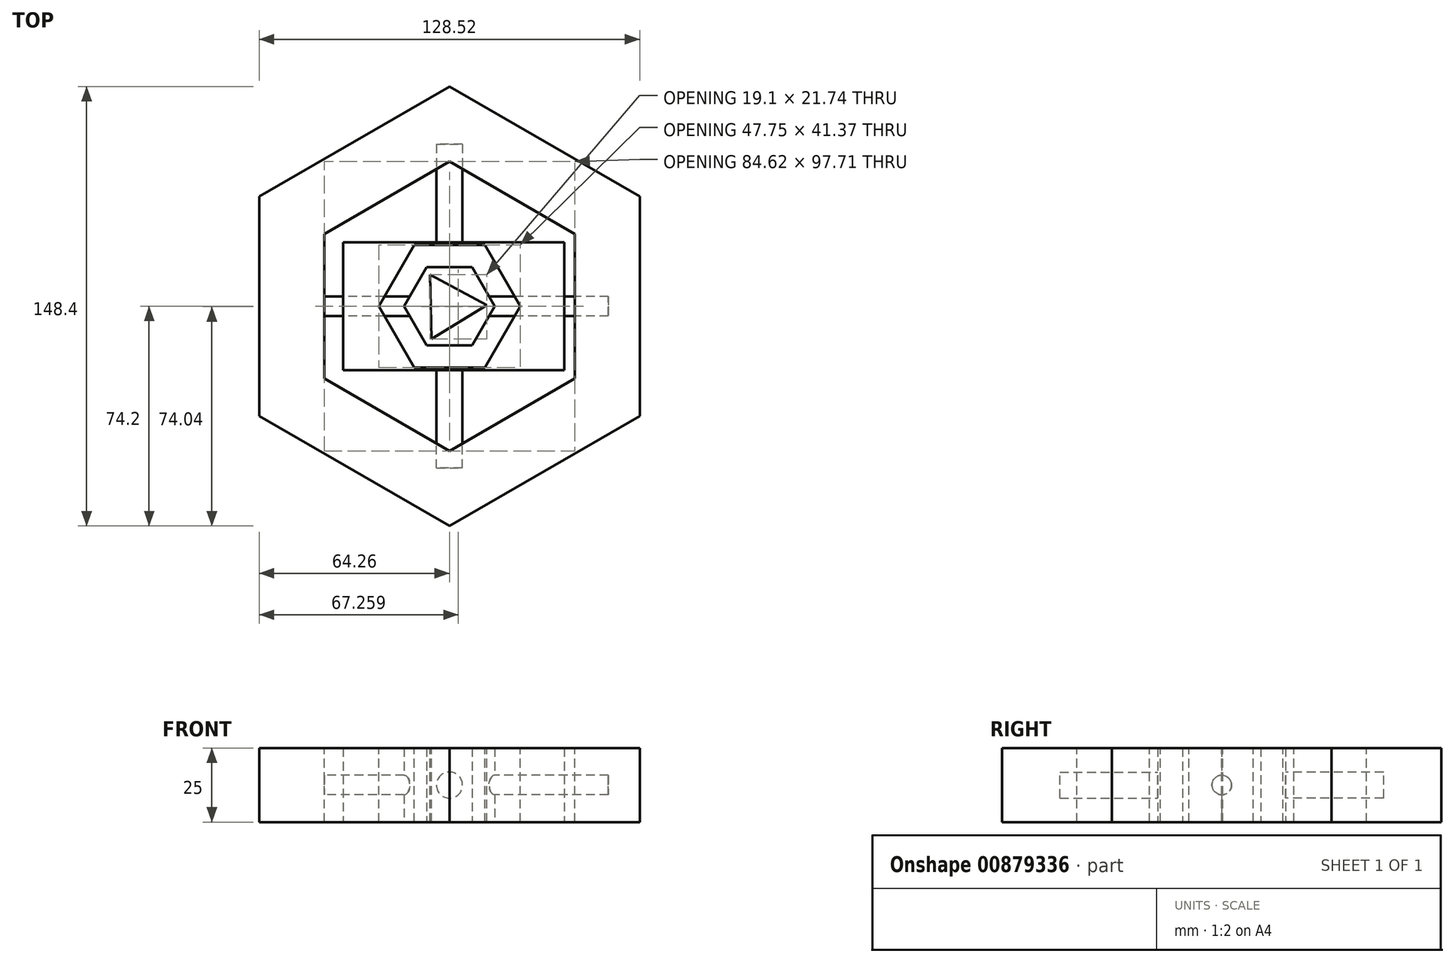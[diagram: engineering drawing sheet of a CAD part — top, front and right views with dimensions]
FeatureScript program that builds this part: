
annotation { "Feature Type Name" : "Feature", "Feature Type Description" : "" }
export const myFeature = defineFeature(function(context is Context, id is Id, definition is map)
    precondition{}
    {
        {
            var Q0;
            Q0=qCreatedBy(makeId("Top.planeOp"),FACE);
            var sketch = newSketch(context, id + "F0", { "sketchPlane" : qUnion([Q0])});
            skCircle(sketch, "E0.cCircle", {"center": v(0, 0) * mm, "radius": 74.2 * mm, "construction": true});
            skLineSegment(sketch, "E0.0", {"start": v(0, 74.2) * mm, "end": v(64.26, 37.1) * mm});
            skLineSegment(sketch, "E0.1", {"start": v(64.26, 37.1) * mm, "end": v(64.26, -37.1) * mm});
            skLineSegment(sketch, "E0.2", {"start": v(64.26, -37.1) * mm, "end": v(0, -74.2) * mm});
            skLineSegment(sketch, "E0.3", {"start": v(0, -74.2) * mm, "end": v(-64.26, -37.1) * mm});
            skLineSegment(sketch, "E0.4", {"start": v(-64.26, -37.1) * mm, "end": v(-64.26, 37.1) * mm});
            skLineSegment(sketch, "E0.5", {"start": v(-64.26, 37.1) * mm, "end": v(0, 74.2) * mm});
            skSolve(sketch);
        }
        {
            var Q0;
            Q0 = qSketchRegion(id + "F0", true);
            extrude(context, id + "F1", {"entities" : qUnion([Q0]), "depth" : 25 * mm, "offsetDistance" : 25 * mm});
        }
        {
            var Q0;
            Q0=makeQuery(id+"F1.opExtrude","CAP_FACE",FACE,{"disambiguationData":[OSD([sQuery(id+"F0.wireOp",EDGE,"E0.0"),sQuery(id+"F0.wireOp",EDGE,"E0.1"),sQuery(id+"F0.wireOp",EDGE,"E0.2"),sQuery(id+"F0.wireOp",EDGE,"E0.3"),sQuery(id+"F0.wireOp",EDGE,"E0.4"),sQuery(id+"F0.wireOp",EDGE,"E0.5")])],"isStart":false});
            var sketch = newSketch(context, id + "F2", { "sketchPlane" : qUnion([Q0])});
            skCircle(sketch, "E1.cCircle", {"center": v(0, 0) * mm, "radius": 48.86 * mm, "construction": true});
            skLineSegment(sketch, "E1.0", {"start": v(0, 48.86) * mm, "end": v(42.31, 24.43) * mm});
            skLineSegment(sketch, "E1.1", {"start": v(42.31, 24.43) * mm, "end": v(42.31, -24.43) * mm});
            skLineSegment(sketch, "E1.2", {"start": v(42.31, -24.43) * mm, "end": v(0, -48.86) * mm});
            skLineSegment(sketch, "E1.3", {"start": v(0, -48.86) * mm, "end": v(-42.31, -24.43) * mm});
            skLineSegment(sketch, "E1.4", {"start": v(-42.31, -24.43) * mm, "end": v(-42.31, 24.43) * mm});
            skLineSegment(sketch, "E1.5", {"start": v(-42.31, 24.43) * mm, "end": v(0, 48.86) * mm});
            skSolve(sketch);
        }
        {
            var Q0;
            Q0 = qSketchRegion(id + "F2", true);
            extrude(context, id + "F3", {"entities" : qUnion([Q0]), "operationType" : NewBodyOperationType.REMOVE, "oppositeDirection" : true, "depth" : 35.3 * mm, "offsetDistance" : 25 * mm});
        }
        {
            var Q0;
            Q0=qCreatedBy(makeId("Top.planeOp"),FACE);
            var sketch = newSketch(context, id + "F4", { "sketchPlane" : qUnion([Q0])});
            skLineSegment(sketch, "E2.bottom", {"start": v(-35.9, -21.57) * mm, "end": v(38.8, -21.57) * mm});
            skLineSegment(sketch, "E2.top", {"start": v(-35.9, 21.57) * mm, "end": v(38.8, 21.57) * mm});
            skLineSegment(sketch, "E2.left", {"start": v(-35.9, -21.57) * mm, "end": v(-35.9, 21.57) * mm});
            skLineSegment(sketch, "E2.right", {"start": v(38.8, -21.57) * mm, "end": v(38.8, 21.57) * mm});
            skPoint(sketch, "E2.middle", {"position": v(1.45, 0) * mm});
            skSolve(sketch);
        }
        {
            var Q0;
            Q0 = qSketchRegion(id + "F4", true);
            extrude(context, id + "F5", {"entities" : qUnion([Q0]), "depth" : 25 * mm, "offsetDistance" : 25 * mm});
        }
        {
            var Q0;
            Q0=makeQuery(id+"F5.opExtrude","SWEPT_FACE",FACE,{"disambiguationData":[OSD([sQuery(id+"F4.wireOp",EDGE,"E2.bottom")])]});
            var sketch = newSketch(context, id + "F6", { "sketchPlane" : qUnion([Q0])});
            skCircle(sketch, "E3", {"center": v(0, 12.48) * mm, "radius": 4.41 * mm});
            skSolve(sketch);
        }
        {
            var Q0;
            Q0 = qSketchRegion(id + "F6", true);
            extrude(context, id + "F7", {"entities" : qUnion([Q0]), "depth" : 33.1 * mm, "offsetDistance" : 25 * mm});
        }
        {
            var Q0;
            Q0=makeQuery(id+"F7.opExtrude","SWEPT_BODY",BODY,{"disambiguationData":[OSD([sQuery(id+"F6.wireOp",EDGE,"E3")])]});
            var Q1;
            Q1=qCreatedBy(makeId("Front.planeOp"),FACE);
            mirror(context, id + "F8", {"entities" : qUnion([Q0]), "mirrorPlane" : qUnion([Q1])});
        }
        {
            var Q0;
            Q0=makeQuery(id+"F5.opExtrude","CAP_FACE",FACE,{"disambiguationData":[OSD([sQuery(id+"F4.wireOp",EDGE,"E2.bottom"),sQuery(id+"F4.wireOp",EDGE,"E2.top"),sQuery(id+"F4.wireOp",EDGE,"E2.left"),sQuery(id+"F4.wireOp",EDGE,"E2.right")])],"isStart":false});
            var sketch = newSketch(context, id + "F9", { "sketchPlane" : qUnion([Q0])});
            skCircle(sketch, "E4.cCircle", {"center": v(0, 0) * mm, "radius": 20.68 * mm, "construction": true});
            skLineSegment(sketch, "E4.0", {"start": v(-23.87, 0.02) * mm, "end": v(-11.92, 20.68) * mm});
            skLineSegment(sketch, "E4.1", {"start": v(-11.92, 20.68) * mm, "end": v(11.95, 20.67) * mm});
            skLineSegment(sketch, "E4.2", {"start": v(11.95, 20.67) * mm, "end": v(23.87, -0.02) * mm});
            skLineSegment(sketch, "E4.3", {"start": v(23.87, -0.02) * mm, "end": v(11.92, -20.68) * mm});
            skLineSegment(sketch, "E4.4", {"start": v(11.92, -20.68) * mm, "end": v(-11.95, -20.67) * mm});
            skLineSegment(sketch, "E4.5", {"start": v(-11.95, -20.67) * mm, "end": v(-23.87, 0.02) * mm});
            skPoint(sketch, "E4.0.midPoint", {"position": v(-17.9, 10.35) * mm});
            skSolve(sketch);
        }
        {
            var Q0;
            Q0 = qSketchRegion(id + "F9", true);
            extrude(context, id + "F10", {"entities" : qUnion([Q0]), "operationType" : NewBodyOperationType.REMOVE, "oppositeDirection" : true, "depth" : 33.1 * mm, "offsetDistance" : 25 * mm});
        }
        {
            var Q0;
            Q0=makeQuery(id+"F3.boolean.opBoolean","COPY",FACE,{"derivedFrom":makeQuery(id+"F3.opExtrude","SWEPT_FACE",FACE,{"disambiguationData":[OSD([sQuery(id+"F2.wireOp",EDGE,"E1.4")])]})});
            var sketch = newSketch(context, id + "F11", { "sketchPlane" : qUnion([Q0])});
            skCircle(sketch, "E5", {"center": v(0.02, 12.5) * mm, "radius": 3.32 * mm});
            skSolve(sketch);
        }
        {
            var Q0;
            Q0 = qSketchRegion(id + "F11", true);
            extrude(context, id + "F12", {"entities" : qUnion([Q0]), "depth" : 96 * mm, "offsetDistance" : 25 * mm});
        }
        {
            var Q0;
            Q0=qCreatedBy(makeId("Top.planeOp"),FACE);
            var sketch = newSketch(context, id + "F13", { "sketchPlane" : qUnion([Q0])});
            skCircle(sketch, "E6.cCircle", {"center": v(0, 0) * mm, "radius": 13.25 * mm, "construction": true});
            skLineSegment(sketch, "E6.0", {"start": v(-7.65, 13.25) * mm, "end": v(7.65, 13.25) * mm});
            skLineSegment(sketch, "E6.1", {"start": v(7.65, 13.25) * mm, "end": v(15.3, 0) * mm});
            skLineSegment(sketch, "E6.2", {"start": v(15.3, 0) * mm, "end": v(7.65, -13.25) * mm});
            skLineSegment(sketch, "E6.3", {"start": v(7.65, -13.25) * mm, "end": v(-7.65, -13.25) * mm});
            skLineSegment(sketch, "E6.4", {"start": v(-7.65, -13.25) * mm, "end": v(-15.3, 0) * mm});
            skLineSegment(sketch, "E6.5", {"start": v(-15.3, 0) * mm, "end": v(-7.65, 13.25) * mm});
            skPoint(sketch, "E6.0.midPoint", {"position": v(0, 13.25) * mm});
            skSolve(sketch);
        }
        {
            var Q0;
            Q0 = qSketchRegion(id + "F13", true);
            extrude(context, id + "F14", {"entities" : qUnion([Q0]), "operationType" : NewBodyOperationType.ADD, "depth" : 25 * mm, "offsetDistance" : 25 * mm});
        }
        {
            var Q0;
            Q0=makeQuery(id+"F14.opExtrude","CAP_FACE",FACE,{"disambiguationData":[OSD([sQuery(id+"F13.wireOp",EDGE,"E6.0"),sQuery(id+"F13.wireOp",EDGE,"E6.1"),sQuery(id+"F13.wireOp",EDGE,"E6.2"),sQuery(id+"F13.wireOp",EDGE,"E6.3"),sQuery(id+"F13.wireOp",EDGE,"E6.4"),sQuery(id+"F13.wireOp",EDGE,"E6.5")])],"isStart":false});
            var sketch = newSketch(context, id + "F15", { "sketchPlane" : qUnion([Q0])});
            skCircle(sketch, "E7.cCircle", {"center": v(0, 0) * mm, "radius": 6.28 * mm, "construction": true});
            skLineSegment(sketch, "E7.0", {"start": v(-6.55, 10.7) * mm, "end": v(12.55, 0.32) * mm});
            skLineSegment(sketch, "E7.1", {"start": v(12.55, 0.32) * mm, "end": v(-6, -11.03) * mm});
            skLineSegment(sketch, "E7.2", {"start": v(-6, -11.03) * mm, "end": v(-6.55, 10.7) * mm});
            skPoint(sketch, "E7.0.midPoint", {"position": v(3, 5.51) * mm});
            skSolve(sketch);
        }
        {
            var Q0;
            Q0 = qSketchRegion(id + "F15", true);
            extrude(context, id + "F16", {"entities" : qUnion([Q0]), "operationType" : NewBodyOperationType.REMOVE, "oppositeDirection" : true, "depth" : 25 * mm, "offsetDistance" : 25 * mm});
        }
    });
